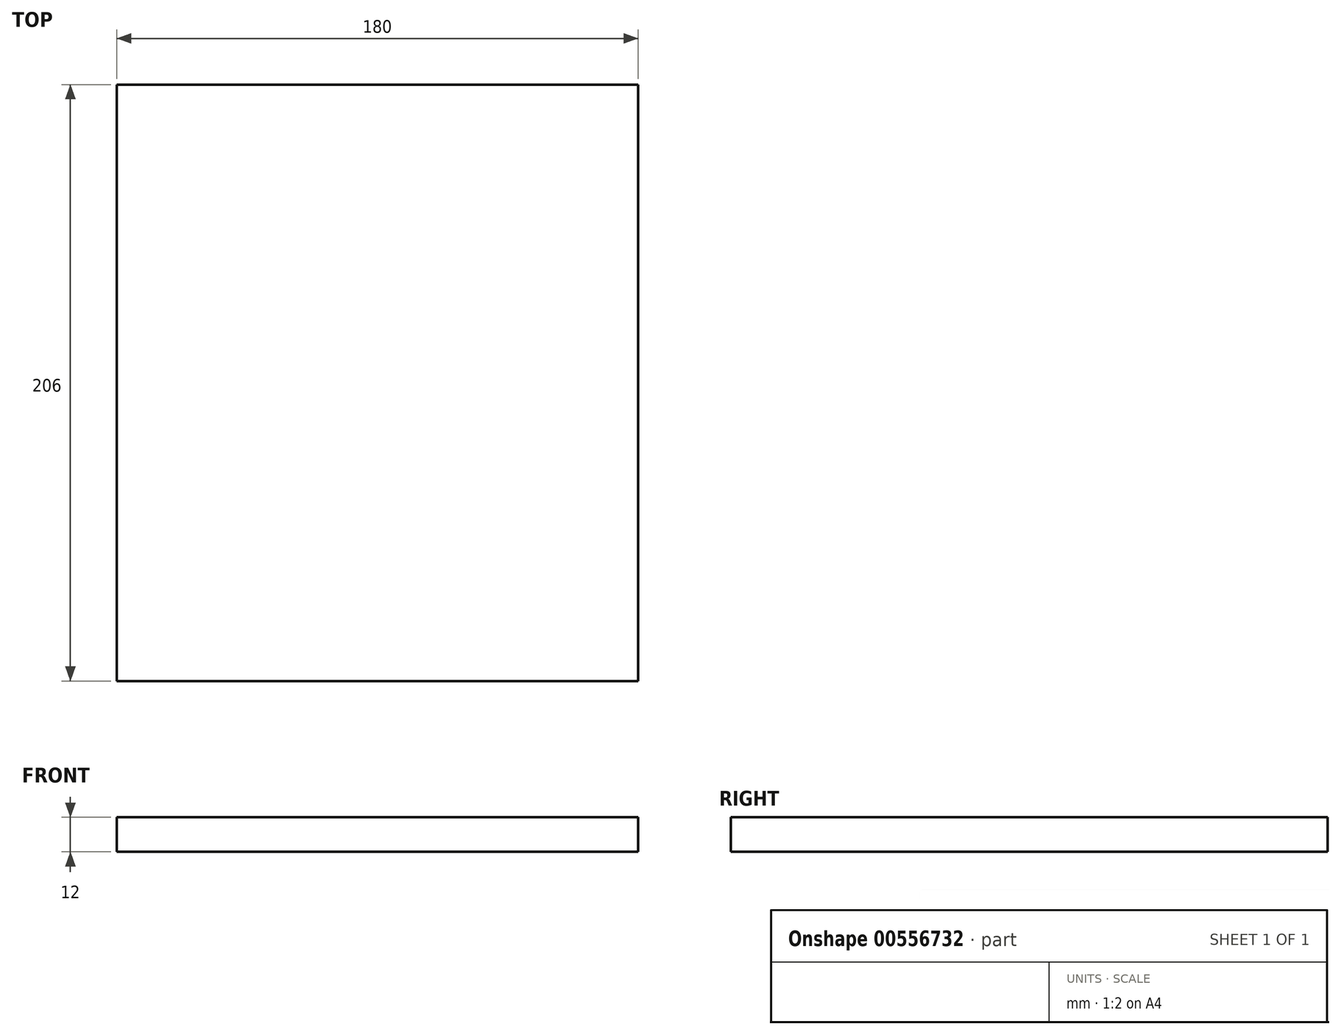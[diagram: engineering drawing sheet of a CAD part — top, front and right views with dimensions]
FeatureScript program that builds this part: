
annotation { "Feature Type Name" : "Feature", "Feature Type Description" : "" }
export const myFeature = defineFeature(function(context is Context, id is Id, definition is map)
    precondition{}
    {
        {
            var Q0;
            Q0=qCreatedBy(makeId("Top.planeOp"),FACE);
            var sketch = newSketch(context, id + "F0", { "sketchPlane" : qUnion([Q0])});
            skLineSegment(sketch, "E0", {"start": v(0, 0) * mm, "end": v(0, 206) * mm});
            skLineSegment(sketch, "E1", {"start": v(0, 206) * mm, "end": v(180, 206) * mm});
            skLineSegment(sketch, "E2", {"start": v(180, 0) * mm, "end": v(180, 206) * mm});
            skLineSegment(sketch, "E3", {"start": v(180, 0) * mm, "end": v(0, 0) * mm});
            skSolve(sketch);
        }
        {
            var Q0;
            Q0=makeQuery(id+"F0.imprint","IMPRINT",FACE,{"disambiguationData":[TD([[makeQuery(id+"F0.imprint","IMPRINT",EDGE,{"derivedFrom":sQuery(id+"F0.wireOp",EDGE,"E0")}),-1.0]])]});
            extrude(context, id + "F1", {"entities" : qUnion([Q0]), "endBound" : BoundingType.SYMMETRIC, "depth" : 12 * mm, "offsetDistance" : 25 * mm});
        }
        {
            var Q0;
            Q0 = qSketchRegion(id + "F0", true);
            extrude(context, id + "F2", {"entities" : qUnion([Q0]), "operationType" : NewBodyOperationType.ADD, "endBound" : BoundingType.SYMMETRIC, "depth" : 12 * mm, "offsetDistance" : 25 * mm});
        }
    });
